# Revit family: ЭВАН ЭПО PRO 36-60 кВт
name_source: partatom
category: Оборудование
units: mm (PartAtom-declared; Revit-internal decimal feet)

## family parameters
Всегда вертикально = Да
Классификация = Нет
На основе рабочей плоскости = Да
Общий = Нет
При загрузке вырезать с полостями = Нет
Размер круглого соединителя = Использовать диаметр
Тип детали = Нормальный
Точка расчета площади = Нет

## types (5) — shared parameters
ADSK_Классификация нагрузок = Прочее
ADSK_Количество фаз = 3
ADSK_Материал = Сталь
ADSK_Номинальная мощность = 0 Вт
ADSK_Размер_Высота = 512 мм
ADSK_Размер_Длина = 715 мм
ADSK_Размер_Ширина = 390 мм
ADSK_Расход теплоносителя = 0.0 м³/ч
Dn = 32 мм
База = ЭЛЕКТРИЧЕСКИЙ ТЕПЛОГЕНЕРАТОР (КОТЕЛ)
Диапазон регулируемых температур теплоносителя, оС = От +30 до +85
Крышка_Видимость = Да
Максимальная температура теплоносителя, оС = +85
Материал корпуса = Сталь
Минимальная температура теплоносителя, оС = +30
Мощность 1-й ступени (по умолчанию) = 0 Вт
Объем колбы котла, л = 50
Рабоча зона_Видимость = Да
Рабочее давление, МПа = 0.1-0.3
Резьба патрубков для подключения трубопроводов теплоносителя = G1 1/4
zero-valued in all types: Отметка по умолчанию

## per-type parameters (varying)
| type | Потребляемая электрическая мощность при максимальной тепловой мощность  в час, кВт/ч |
| ЭВАН ЭПО PRO - 36 кВт | 39.6 |
| ЭВАН ЭПО PRO - 42 кВт | 44.1 |
| ЭВАН ЭПО PRO - 48 кВт | 50.4 |
| ЭВАН ЭПО PRO - 54 кВт | 56.7 |
| ЭВАН ЭПО PRO - 60 кВт | 56.7 |
